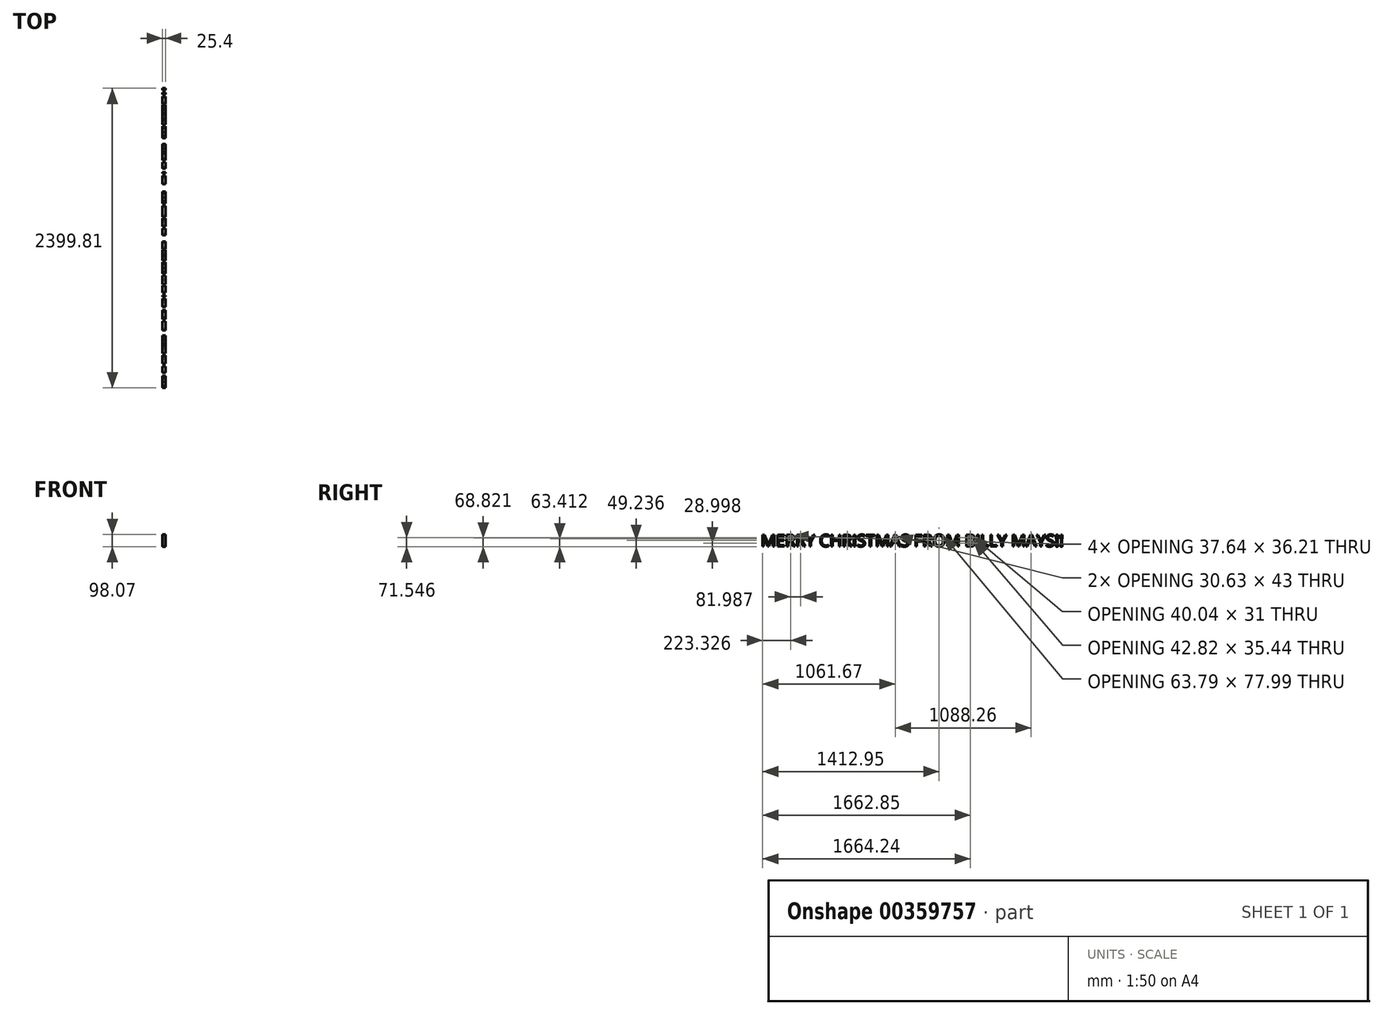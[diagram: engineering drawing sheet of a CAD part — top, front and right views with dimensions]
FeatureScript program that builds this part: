
annotation { "Feature Type Name" : "Feature", "Feature Type Description" : "" }
export const myFeature = defineFeature(function(context is Context, id is Id, definition is map)
    precondition{}
    {
        {
            var Q0;
            Q0=qCreatedBy(makeId("Right.planeOp"),FACE);
            var sketch = newSketch(context, id + "F0", { "sketchPlane" : qUnion([Q0])});
            skText(sketch, "E0", { "text": "MERRY CHRISTMAS FROM BILLY MAYS!!", "fontName": "OpenSans-Regular.ttf"});
            const initialGuessF0  = {"E0": [-0.66276, -0.06866, 1, 0, 0.0955]};
            skSetInitialGuess(sketch, initialGuessF0);
            skSolve(sketch);
        }
        {
            var Q0;
            Q0 = qSketchRegion(id + "F0", true);
            extrude(context, id + "F1", {"entities" : qUnion([Q0]), "depth" : 25.4 * mm});
        }
    });
